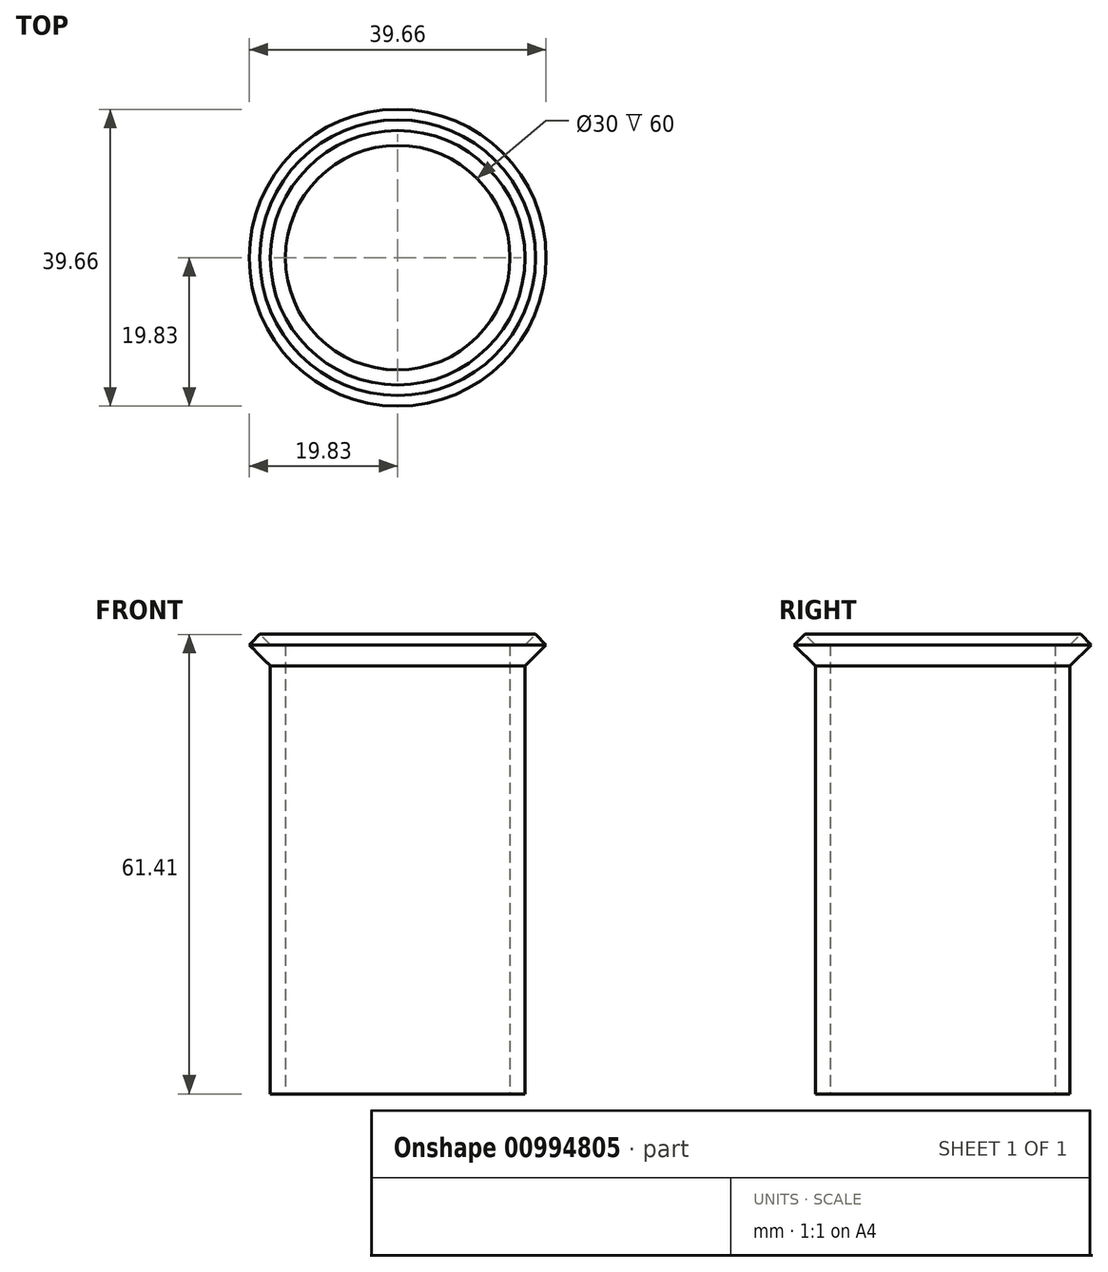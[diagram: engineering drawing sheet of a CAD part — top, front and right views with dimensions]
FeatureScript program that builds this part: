
annotation { "Feature Type Name" : "Feature", "Feature Type Description" : "" }
export const myFeature = defineFeature(function(context is Context, id is Id, definition is map)
    precondition{}
    {
        {
            var Q0;
            Q0=qCreatedBy(makeId("Front.planeOp"),FACE);
            var sketch = newSketch(context, id + "F0", { "sketchPlane" : qUnion([Q0])});
            skLineSegment(sketch, "E0", {"start": v(15, 60) * mm, "end": v(15, 0) * mm});
            skPoint(sketch, "E1.orphan", {"position": v(15, 0) * mm});
            skLineSegment(sketch, "E2.0", {"start": v(17, 60) * mm, "end": v(17, 0) * mm});
            skLineSegment(sketch, "E3", {"start": v(15, 60) * mm, "end": v(17, 60) * mm});
            skLineSegment(sketch, "E4", {"start": v(0, 0) * mm, "end": v(0, 111.14) * mm});
            skLineSegment(sketch, "E5", {"start": v(15, 0) * mm, "end": v(17, 0) * mm});
            skLineSegment(sketch, "E6", {"start": v(17, 60) * mm, "end": v(18.41, 61.41) * mm});
            skLineSegment(sketch, "E7", {"start": v(18.41, 61.41) * mm, "end": v(19.83, 60) * mm});
            skLineSegment(sketch, "E8", {"start": v(19.83, 60) * mm, "end": v(17, 57.17) * mm});
            skSolve(sketch);
        }
        {
            var Q0;
            Q0=qSketchRegion(id+"F0",true);
            var Q1;
            Q1=sQuery(id+"F0.wireOp",EDGE,"E4");
            revolve(context, id + "F1", {"surfaceOperationType" : NewSurfaceOperationType.NEW, "entities" : qUnion([Q0]), "axis" : qUnion([Q1]), "revolveType" : RevolveType.FULL});
        }
    });
